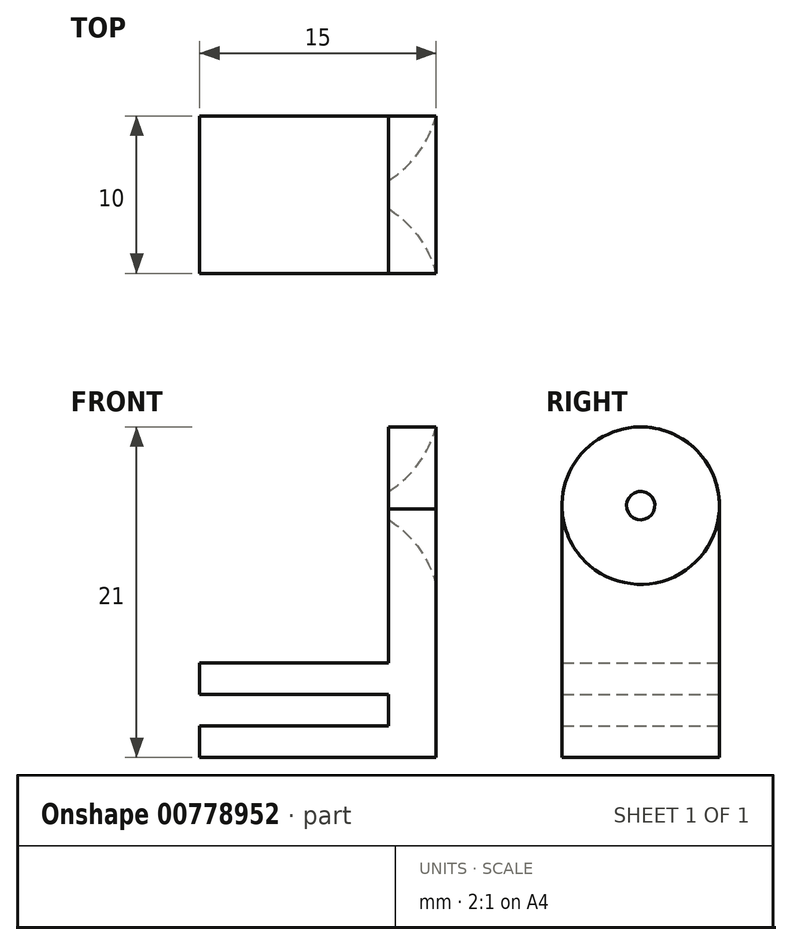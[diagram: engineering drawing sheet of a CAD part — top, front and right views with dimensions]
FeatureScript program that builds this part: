
annotation { "Feature Type Name" : "Feature", "Feature Type Description" : "" }
export const myFeature = defineFeature(function(context is Context, id is Id, definition is map)
    precondition{}
    {
        {
            var Q0;
            Q0=qCreatedBy(makeId("Front.planeOp"),FACE);
            var sketch = newSketch(context, id + "F0", { "sketchPlane" : qUnion([Q0])});
            skLineSegment(sketch, "E0.bottom", {"start": v(0, 0) * mm, "end": v(15, 0) * mm});
            skLineSegment(sketch, "E0.top", {"start": v(0, 6) * mm, "end": v(12, 6) * mm});
            skLineSegment(sketch, "E0.left", {"start": v(0, 0) * mm, "end": v(0, 2) * mm});
            skLineSegment(sketch, "E0.right", {"start": v(15, 0) * mm, "end": v(15, 6) * mm});
            skLineSegment(sketch, "E1.bottom", {"start": v(0, 0) * mm, "end": v(12, 0) * mm});
            skLineSegment(sketch, "E1.top", {"start": v(0, 2) * mm, "end": v(12, 2) * mm});
            skLineSegment(sketch, "E2.top", {"start": v(0, 4) * mm, "end": v(12, 4) * mm});
            skLineSegment(sketch, "E2.left", {"start": v(0, 6) * mm, "end": v(0, 4) * mm});
            skLineSegment(sketch, "E3.top", {"start": v(12, 21) * mm, "end": v(15, 21) * mm});
            skLineSegment(sketch, "E3.left", {"start": v(12, 6) * mm, "end": v(12, 21) * mm});
            skLineSegment(sketch, "E3.right", {"start": v(15, 6) * mm, "end": v(15, 21) * mm});
            skLineSegment(sketch, "E4", {"start": v(12, 2) * mm, "end": v(12, 4) * mm});
            skLineSegment(sketch, "E5.trimOffspring", {"start": v(0, 4) * mm, "end": v(0, 6) * mm});
            skSolve(sketch);
        }
        {
            var Q0;
            Q0=makeQuery(id+"F0.imprint","IMPRINT",FACE,{"disambiguationData":[TD([[makeQuery(id+"F0.imprint","IMPRINT",EDGE,{"derivedFrom":sQuery(id+"F0.wireOp",EDGE,"E0.bottom")}),1.0]])]});
            extrude(context, id + "F1", {"entities" : qUnion([Q0]), "depth" : 20 * mm, "offsetDistance" : 25 * mm});
        }
        {
            var Q0;
            Q0=makeQuery(id+"F1.opExtrude","SWEPT_FACE",FACE,{"disambiguationData":[OSD([sQuery(id+"F0.wireOp",EDGE,"E3.left")])]});
            var sketch = newSketch(context, id + "F2", { "sketchPlane" : qUnion([Q0])});
            skCircle(sketch, "E6", {"center": v(10, 16) * mm, "radius": 5 * mm});
            skPoint(sketch, "E6.centerSnap0", {"position": v(10, 6) * mm});
            skCircle(sketch, "E7", {"center": v(10, 16) * mm, "radius": 0.9 * mm});
            skLineSegment(sketch, "E8", {"start": v(15, 15.78) * mm, "end": v(15, 0) * mm});
            skLineSegment(sketch, "E9", {"start": v(5, 15.77) * mm, "end": v(5, 0) * mm});
            skSolve(sketch);
        }
        {
            var Q0;
            {var subQ0=sQuery(id+"F0.wireOp",EDGE,"E3.left");var subQ1=makeQuery(id+"F1.opExtrude","CAP_EDGE",EDGE,{"disambiguationData":[OSD([subQ0])],"isStart":false});Q0=makeQuery(id+"F2.imprint","IMPRINT",FACE,{"disambiguationData":[TD([[makeQuery(id+"F2.imprint","IMPRINT",EDGE,{"derivedFrom":subQ1}),1.0]])]});}
            var Q1;
            {var subQ0=sQuery(id+"F0.wireOp",EDGE,"E3.left");var subQ1=makeQuery(id+"F1.opExtrude","CAP_EDGE",EDGE,{"disambiguationData":[OSD([subQ0])],"isStart":true});Q1=makeQuery(id+"F2.imprint","IMPRINT",FACE,{"disambiguationData":[TD([[makeQuery(id+"F2.imprint","IMPRINT",EDGE,{"derivedFrom":subQ1}),-1.0]])]});}
            extrude(context, id + "F3", {"entities" : qUnion([Q0, Q1]), "operationType" : NewBodyOperationType.REMOVE, "endBound" : BoundingType.THROUGH_ALL, "oppositeDirection" : true, "depth" : 25 * mm, "offsetDistance" : 25 * mm});
        }
        {
            var Q0;
            Q0=makeQuery(id+"F1.opExtrude","SWEPT_FACE",FACE,{"disambiguationData":[OSD([sQuery(id+"F0.wireOp",EDGE,"E0.right"),sQuery(id+"F0.wireOp",EDGE,"E3.right")])]});
            var sketch = newSketch(context, id + "F4", { "sketchPlane" : qUnion([Q0])});
            skLineSegment(sketch, "E10", {"start": v(-15, 6) * mm, "end": v(-15, 0) * mm});
            skLineSegment(sketch, "E11", {"start": v(-5, 6) * mm, "end": v(-5, 0) * mm});
            skSolve(sketch);
        }
        {
            var Q0;
            {var subQ0=sQuery(id+"F4.wireOp",EDGE,"E11");Q0=makeQuery(id+"F4.imprint","IMPRINT",FACE,{"disambiguationData":[TD([[makeQuery(id+"F4.imprint","IMPRINT",EDGE,{"derivedFrom":subQ0}),1.0]])]});}
            var Q1;
            {var subQ0=sQuery(id+"F4.wireOp",EDGE,"E10");Q1=makeQuery(id+"F4.imprint","IMPRINT",FACE,{"disambiguationData":[TD([[makeQuery(id+"F4.imprint","IMPRINT",EDGE,{"derivedFrom":subQ0}),-1.0]])]});}
            extrude(context, id + "F5", {"entities" : qUnion([Q0, Q1]), "operationType" : NewBodyOperationType.REMOVE, "endBound" : BoundingType.THROUGH_ALL, "oppositeDirection" : true, "depth" : 25 * mm, "offsetDistance" : 25 * mm});
        }
        {
            var Q0;
            Q0=makeQuery(id+"F2.imprint","IMPRINT",FACE,{"disambiguationData":[TD([[makeQuery(id+"F2.imprint","IMPRINT",EDGE,{"derivedFrom":sQuery(id+"F2.wireOp",EDGE,"E7")}),1.0]])]});
            extrude(context, id + "F6", {"entities" : qUnion([Q0]), "operationType" : NewBodyOperationType.REMOVE, "endBound" : BoundingType.THROUGH_ALL, "oppositeDirection" : true, "depth" : 25 * mm, "offsetDistance" : 25 * mm});
        }
        {
            var Q0;
            Q0=makeQuery(id+"F1.opExtrude","SWEPT_FACE",FACE,{"disambiguationData":[OSD([sQuery(id+"F0.wireOp",EDGE,"E0.right"),sQuery(id+"F0.wireOp",EDGE,"E3.right")])]});
            var sketch = newSketch(context, id + "F7", { "sketchPlane" : qUnion([Q0])});
            skCircle(sketch, "E12", {"center": v(-10, 16) * mm, "radius": 5 * mm});
            skLineSegment(sketch, "E13", {"start": v(-10, 21) * mm, "end": v(-10, 9.58) * mm});
            skPoint(sketch, "E13.startSnap0", {"position": v(-10, 21) * mm});
            skSolve(sketch);
        }
        {
            var Q0;
            Q0=makeQuery(id+"F5.boolean.opBoolean","MERGE",FACE,{"derivedFrom":[makeQuery(id+"F3.boolean.opBoolean","COPY",FACE,{"derivedFrom":makeQuery(id+"F3.opExtrude","SWEPT_FACE",FACE,{"disambiguationData":[OSD([sQuery(id+"F2.wireOp",EDGE,"E8")])]})}),makeQuery(id+"F5.opExtrude","SWEPT_FACE",FACE,{"disambiguationData":[OSD([sQuery(id+"F4.wireOp",EDGE,"E10")])]})]});
            var Q1;
            Q1=makeQuery(id+"F5.boolean.opBoolean","MERGE",FACE,{"derivedFrom":[makeQuery(id+"F3.boolean.opBoolean","COPY",FACE,{"derivedFrom":makeQuery(id+"F3.opExtrude","SWEPT_FACE",FACE,{"disambiguationData":[OSD([sQuery(id+"F2.wireOp",EDGE,"E9")])]})}),makeQuery(id+"F5.opExtrude","SWEPT_FACE",FACE,{"disambiguationData":[OSD([sQuery(id+"F4.wireOp",EDGE,"E11")])]})]});
            cPlane(context, id + "F8", {"entities" : qUnion([Q0, Q1]), "cplaneType" : CPlaneType.MID_PLANE, "offset" : 25 * mm, "width" : 150 * mm, "height" : 150 * mm});
        }
        {
            var Q0;
            Q0=qCreatedBy(id+"F8.planeOp",FACE);
            var sketch = newSketch(context, id + "F9", { "sketchPlane" : qUnion([Q0])});
            skLineSegment(sketch, "E14", {"start": v(12, 16) * mm, "end": v(15, 16) * mm});
            skLineSegment(sketch, "E15", {"start": v(15, 16.9) * mm, "end": v(15, 21) * mm});
            skArc(sketch, "E16", {"start": v(12, 16.9) * mm, "mid": v(13.89, 18.66) * mm, "end": v(15, 21) * mm});
            skLineSegment(sketch, "E17", {"start": v(12, 16.9) * mm, "end": v(15, 16.9) * mm});
            skSolve(sketch);
        }
        {
            var Q0;
            Q0 = qSketchRegion(id + "F9", true);
            var Q1;
            Q1=sQuery(id+"F9.wireOp",EDGE,"E15");
            var Q2;
            Q2=sQuery(id+"F9.wireOp",EDGE,"E16");
            var Q3;
            Q3=sQuery(id+"F9.wireOp",EDGE,"E17");
            var Q4;
            Q4=sQuery(id+"F9.wireOp",EDGE,"E14");
            revolve(context, id + "F10", {"operationType" : NewBodyOperationType.REMOVE, "surfaceOperationType" : NewSurfaceOperationType.NEW, "entities" : qUnion([Q0]), "surfaceEntities" : qUnion([Q1, Q2, Q3]), "axis" : qUnion([Q4]), "revolveType" : RevolveType.FULL, "oppositeDirection" : true});
        }
    });
